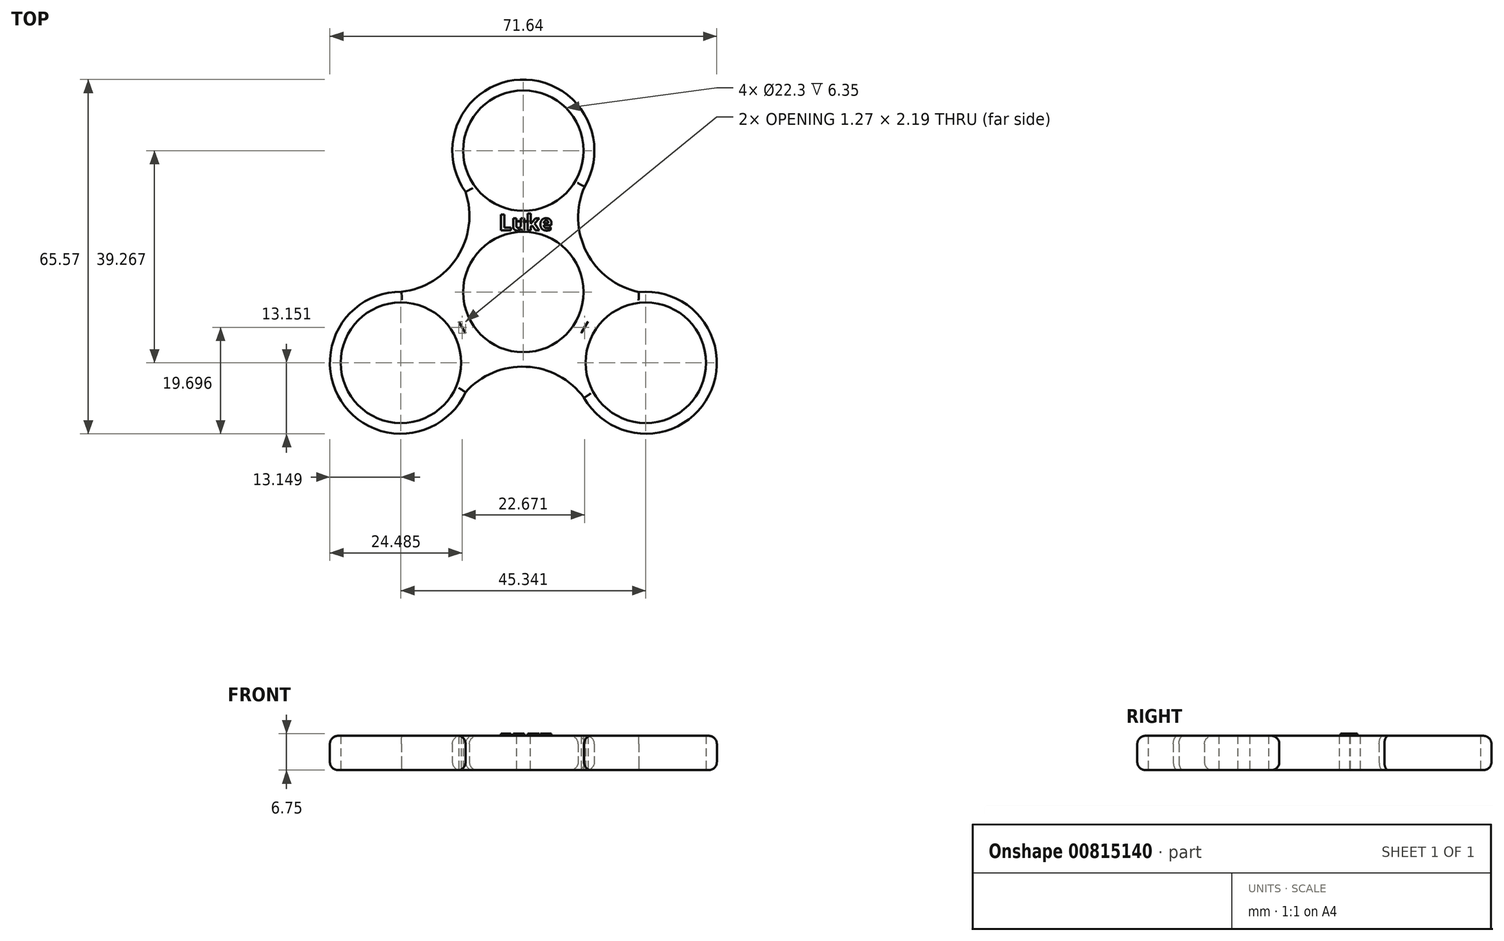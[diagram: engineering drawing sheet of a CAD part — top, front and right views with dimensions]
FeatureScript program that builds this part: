
annotation { "Feature Type Name" : "Feature", "Feature Type Description" : "" }
export const myFeature = defineFeature(function(context is Context, id is Id, definition is map)
    precondition{}
    {
        {
            var Q0;
            Q0=qCreatedBy(makeId("Top.planeOp"),FACE);
            var sketch = newSketch(context, id + "F0", { "sketchPlane" : qUnion([Q0])});
            skCircle(sketch, "E0", {"center": v(0, 0) * mm, "radius": 11.15 * mm});
            skArc(sketch, "E1", {"start": v(1.27, 13.09) * mm, "mid": v(0, 13.15) * mm, "end": v(-1.27, 13.09) * mm});
            skCircle(sketch, "E2", {"center": v(0, 26.18) * mm, "radius": 11.15 * mm});
            skArc(sketch, "E3", {"start": v(11.34, 19.51) * mm, "mid": v(-0.58, 39.31) * mm, "end": v(-10.7, 18.54) * mm});
            skArc(sketch, "E4.1.0", {"start": v(-10.7, -7.64) * mm, "mid": v(-11.28, -6.51) * mm, "end": v(-11.97, -5.45) * mm});
            skCircle(sketch, "E4.1.1", {"center": v(-22.67, -13.09) * mm, "radius": 11.15 * mm});
            skArc(sketch, "E4.2.0", {"start": v(11.23, -19.57) * mm, "mid": v(34.34, -19.15) * mm, "end": v(21.4, 0) * mm});
            skCircle(sketch, "E4.2.1", {"center": v(22.67, -13.09) * mm, "radius": 11.15 * mm});
            skArc(sketch, "E5", {"start": v(11.34, 19.51) * mm, "mid": v(11.71, 7.35) * mm, "end": v(21.4, 0) * mm});
            skArc(sketch, "E6.1.0", {"start": v(-22.57, 0.06) * mm, "mid": v(-12.23, 6.47) * mm, "end": v(-10.7, 18.54) * mm});
            skArc(sketch, "E6.2.0", {"start": v(11.23, -19.57) * mm, "mid": v(0.51, -13.82) * mm, "end": v(-10.7, -18.54) * mm});
            skArc(sketch, "E7.trimOffspring", {"start": v(-1.27, 13.09) * mm, "mid": v(0, 13.03) * mm, "end": v(1.27, 13.09) * mm});
            skArc(sketch, "E8.trimOffspring", {"start": v(10.7, -7.64) * mm, "mid": v(11.39, -6.58) * mm, "end": v(11.97, -5.45) * mm});
            skArc(sketch, "E9.trimOffspring", {"start": v(-11.97, -5.45) * mm, "mid": v(-11.39, -6.58) * mm, "end": v(-10.7, -7.64) * mm});
            skArc(sketch, "E10.trimOffspring", {"start": v(-22.57, 0.06) * mm, "mid": v(-33.76, -20.16) * mm, "end": v(-10.7, -18.54) * mm});
            skArc(sketch, "E11.trimOffspring", {"start": v(11.97, -5.45) * mm, "mid": v(11.28, -6.51) * mm, "end": v(10.7, -7.64) * mm});
            skSolve(sketch);
        }
        {
            var Q0;
            Q0=makeQuery(id+"F0.imprint","IMPRINT",FACE,{"disambiguationData":[TD([[makeQuery(id+"F0.imprint","IMPRINT",EDGE,{"derivedFrom":sQuery(id+"F0.wireOp",EDGE,"E0")}),-1.0]])]});
            extrude(context, id + "F1", {"entities" : qUnion([Q0]), "depth" : 6.35 * mm, "offsetDistance" : 25 * mm});
        }
        {
            var Q0;
            Q0=makeQuery(id+"F1.opExtrude","CAP_EDGE",EDGE,{"disambiguationData":[OSD([sQuery(id+"F0.wireOp",EDGE,"E10.trimOffspring")])],"isStart":false});
            var Q1;
            Q1=makeQuery(id+"F1.opExtrude","CAP_EDGE",EDGE,{"disambiguationData":[OSD([sQuery(id+"F0.wireOp",EDGE,"E6.1.0")])],"isStart":false});
            var Q2;
            Q2=makeQuery(id+"F1.opExtrude","CAP_EDGE",EDGE,{"disambiguationData":[OSD([sQuery(id+"F0.wireOp",EDGE,"E3")])],"isStart":false});
            var Q3;
            Q3=makeQuery(id+"F1.opExtrude","CAP_EDGE",EDGE,{"disambiguationData":[OSD([sQuery(id+"F0.wireOp",EDGE,"E6.2.0")])],"isStart":false});
            var Q4;
            Q4=makeQuery(id+"F1.opExtrude","CAP_EDGE",EDGE,{"disambiguationData":[OSD([sQuery(id+"F0.wireOp",EDGE,"E4.2.0")])],"isStart":false});
            var Q5;
            Q5=makeQuery(id+"F1.opExtrude","CAP_EDGE",EDGE,{"disambiguationData":[OSD([sQuery(id+"F0.wireOp",EDGE,"E5")])],"isStart":false});
            var Q6;
            Q6=makeQuery(id+"F1.opExtrude","CAP_EDGE",EDGE,{"disambiguationData":[OSD([sQuery(id+"F0.wireOp",EDGE,"E4.2.0")])],"isStart":true});
            var Q7;
            Q7=makeQuery(id+"F1.opExtrude","CAP_EDGE",EDGE,{"disambiguationData":[OSD([sQuery(id+"F0.wireOp",EDGE,"E5")])],"isStart":true});
            var Q8;
            Q8=makeQuery(id+"F1.opExtrude","CAP_EDGE",EDGE,{"disambiguationData":[OSD([sQuery(id+"F0.wireOp",EDGE,"E3")])],"isStart":true});
            var Q9;
            Q9=makeQuery(id+"F1.opExtrude","CAP_EDGE",EDGE,{"disambiguationData":[OSD([sQuery(id+"F0.wireOp",EDGE,"E6.1.0")])],"isStart":true});
            var Q10;
            Q10=makeQuery(id+"F1.opExtrude","CAP_EDGE",EDGE,{"disambiguationData":[OSD([sQuery(id+"F0.wireOp",EDGE,"E10.trimOffspring")])],"isStart":true});
            var Q11;
            Q11=makeQuery(id+"F1.opExtrude","CAP_EDGE",EDGE,{"disambiguationData":[OSD([sQuery(id+"F0.wireOp",EDGE,"E6.2.0")])],"isStart":true});
            fillet(context, id + "F2", {"entities" : qUnion([Q0, Q1, Q2, Q3, Q4, Q5, Q6, Q7, Q8, Q9, Q10, Q11]), "radius" : 1.5 * mm, "tangentPropagation" : true, "allowEdgeOverflow" : false});
        }
        {
            var Q0;
            Q0=makeQuery(id+"F1.opExtrude","CAP_FACE",FACE,{"disambiguationData":[OSD([sQuery(id+"F0.wireOp",EDGE,"E0"),sQuery(id+"F0.wireOp",EDGE,"E1"),sQuery(id+"F0.wireOp",EDGE,"E2"),sQuery(id+"F0.wireOp",EDGE,"E3"),sQuery(id+"F0.wireOp",EDGE,"E4.1.0"),sQuery(id+"F0.wireOp",EDGE,"E4.1.1"),sQuery(id+"F0.wireOp",EDGE,"E4.2.0"),sQuery(id+"F0.wireOp",EDGE,"E4.2.1"),sQuery(id+"F0.wireOp",EDGE,"E5"),sQuery(id+"F0.wireOp",EDGE,"E6.1.0"),sQuery(id+"F0.wireOp",EDGE,"E6.2.0"),sQuery(id+"F0.wireOp",EDGE,"E7.trimOffspring"),sQuery(id+"F0.wireOp",EDGE,"E8.trimOffspring"),sQuery(id+"F0.wireOp",EDGE,"E9.trimOffspring"),sQuery(id+"F0.wireOp",EDGE,"E10.trimOffspring"),sQuery(id+"F0.wireOp",EDGE,"E11.trimOffspring")])],"isStart":false});
            var sketch = newSketch(context, id + "F3", { "sketchPlane" : qUnion([Q0])});
            skText(sketch, "E12", { "text": "Luke", "fontName": "OpenSans-Bold.ttf"});
            const initialGuessF3  = {"E12": [-0.00449, 0.01142, 1, 0, 0.00292]};
            skSetInitialGuess(sketch, initialGuessF3);
            skSolve(sketch);
        }
        {
            var Q0;
            Q0 = qSketchRegion(id + "F3", true);
            extrude(context, id + "F4", {"entities" : qUnion([Q0]), "operationType" : NewBodyOperationType.ADD, "depth" : 0.4 * mm, "offsetDistance" : 25.4 * mm});
        }
    });
